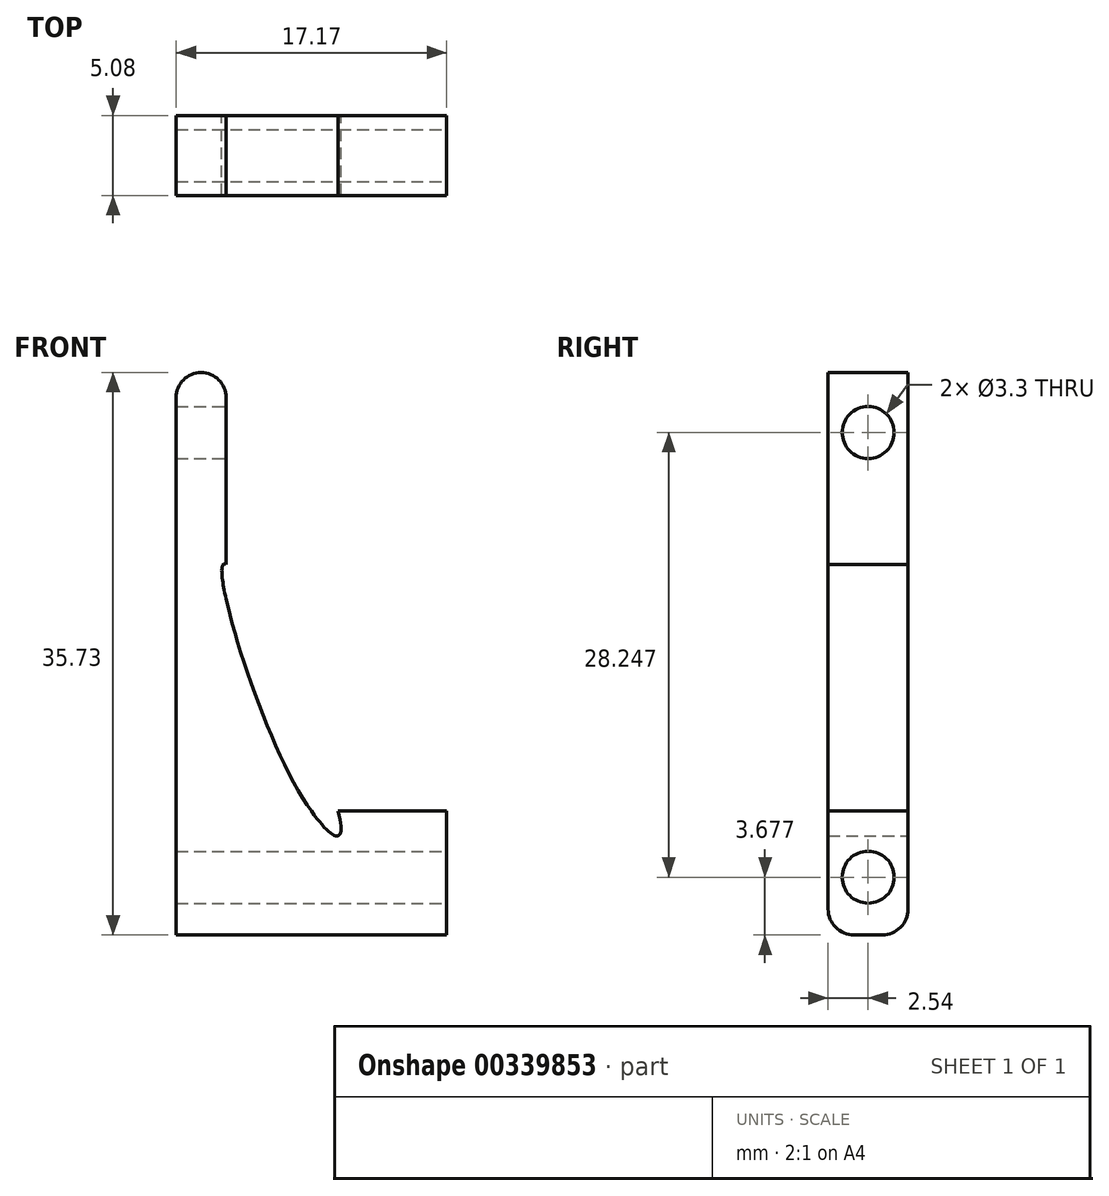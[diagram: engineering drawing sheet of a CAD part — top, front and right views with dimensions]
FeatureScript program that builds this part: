
annotation { "Feature Type Name" : "Feature", "Feature Type Description" : "" }
export const myFeature = defineFeature(function(context is Context, id is Id, definition is map)
    precondition{}
    {
        {
            var Q0;
            Q0=qCreatedBy(makeId("Front.planeOp"),FACE);
            var sketch = newSketch(context, id + "F0", { "sketchPlane" : qUnion([Q0])});
            skLineSegment(sketch, "E0", {"start": v(-26.62, 37.14) * mm, "end": v(-26.62, 44.22) * mm});
            skLineSegment(sketch, "E1", {"start": v(-23.45, 44.22) * mm, "end": v(-23.45, 37.14) * mm});
            skLineSegment(sketch, "E2", {"start": v(-25.04, 45.42) * mm, "end": v(-24.64, 45.42) * mm});
            skFitSpline(sketch, "E3.MirrorCS", {"points": [v(-16.15, 22.5) * mm, v(-19.25, 25.66) * mm, v(-23.45, 39.33) * mm, v(-16.15, 22.5) * mm]});
            skLineSegment(sketch, "E4", {"start": v(-26.62, 15.8) * mm, "end": v(-18.03, 15.8) * mm});
            skLineSegment(sketch, "E5", {"start": v(-26.62, 37.14) * mm, "end": v(-26.62, 15.8) * mm});
            skLineSegment(sketch, "E6", {"start": v(-18.03, 23.66) * mm, "end": v(-9.45, 23.66) * mm});
            skLineSegment(sketch, "E7", {"start": v(-9.45, 23.66) * mm, "end": v(-9.45, 15.8) * mm});
            skLineSegment(sketch, "E8", {"start": v(-9.45, 15.8) * mm, "end": v(-18.03, 15.8) * mm});
            skPoint(sketch, "E9.orphan", {"position": v(-32.26, 15.8) * mm});
            skLineSegment(sketch, "E10", {"start": v(-26.62, 44.22) * mm, "end": v(-26.62, 49.93) * mm});
            skLineSegment(sketch, "E11", {"start": v(-23.45, 49.93) * mm, "end": v(-23.45, 44.22) * mm});
            skArc(sketch, "E12", {"start": v(-23.45, 49.93) * mm, "mid": v(-25.04, 51.52) * mm, "end": v(-26.62, 49.93) * mm});
            skSolve(sketch);
        }
        {
            var Q0;
            Q0=makeQuery(id+"F0.imprint","IMPRINT",FACE,{"disambiguationData":[TD([[makeQuery(id+"F0.imprint","IMPRINT",EDGE,{"derivedFrom":sQuery(id+"F0.wireOp",EDGE,"E0")}),-1.0]])]});
            extrude(context, id + "F1", {"entities" : qUnion([Q0]), "depth" : 5.08 * mm});
        }
        {
            var Q0;
            Q0=makeQuery(id+"F1.opExtrude","CAP_EDGE",EDGE,{"disambiguationData":[OSD([sQuery(id+"F0.wireOp",EDGE,"E4"),sQuery(id+"F0.wireOp",EDGE,"E8")])],"isStart":false});
            var Q1;
            Q1=makeQuery(id+"F1.opExtrude","CAP_EDGE",EDGE,{"disambiguationData":[OSD([sQuery(id+"F0.wireOp",EDGE,"E4"),sQuery(id+"F0.wireOp",EDGE,"E8")])],"isStart":true});
            fillet(context, id + "F2", {"entities" : qUnion([Q0, Q1]), "radius" : 1.65 * mm, "tangentPropagation" : true, "allowEdgeOverflow" : false});
        }
        {
            var Q0;
            Q0=makeQuery(id+"F1.opExtrude","SWEPT_FACE",FACE,{"disambiguationData":[OSD([sQuery(id+"F0.wireOp",EDGE,"E0"),sQuery(id+"F0.wireOp",EDGE,"E5"),sQuery(id+"F0.wireOp",EDGE,"E10")])]});
            var sketch = newSketch(context, id + "F3", { "sketchPlane" : qUnion([Q0])});
            skCircle(sketch, "E13", {"center": v(2.54, 19.47) * mm, "radius": 1.8 * mm});
            skCircle(sketch, "E14", {"center": v(2.54, 47.71) * mm, "radius": 1.75 * mm});
            skSolve(sketch);
        }
        {
            var Q0;
            Q0=sQuery(id+"F3.wireOp",VERTEX,"E14.center");
            var Q1;
            Q1=sQuery(id+"F3.wireOp",VERTEX,"E13.center");
            var Q2;
            Q2=makeQuery(id+"F1.opExtrude","SWEPT_BODY",BODY,{"disambiguationData":[OSD([sQuery(id+"F0.wireOp",EDGE,"E0"),sQuery(id+"F0.wireOp",EDGE,"E1"),sQuery(id+"F0.wireOp",EDGE,"E3.MirrorCS"),sQuery(id+"F0.wireOp",EDGE,"E4"),sQuery(id+"F0.wireOp",EDGE,"E5"),sQuery(id+"F0.wireOp",EDGE,"E6"),sQuery(id+"F0.wireOp",EDGE,"E7"),sQuery(id+"F0.wireOp",EDGE,"E8"),sQuery(id+"F0.wireOp",EDGE,"E10"),sQuery(id+"F0.wireOp",EDGE,"E11"),sQuery(id+"F0.wireOp",EDGE,"E12")])]});
            hole(context, id + "F4", {"style" : HoleStyle.SIMPLE, "endStyle" : HoleEndStyle.THROUGH, "standardTappedOrClearance" : lookupTablePath({ "standard" : "ISO", "fit" : "Normal", "size" : "M3", "type" : "Clearance" }), "standardBlindInLast" : lookupTablePath({ "fit" : "Standard", "standard" : "ISO", "size" : "M3", "type" : "Clearance" }), "holeDiameter" : 3.3 * mm, "isTappedThrough" : true, "tappedDepth" : 12.7 * mm, "tapClearance" : 3, "locations" : qUnion([Q0, Q1]), "scope" : qUnion([Q2]), "startStyle" : HoleStartStyle.PART});
        }
    });
